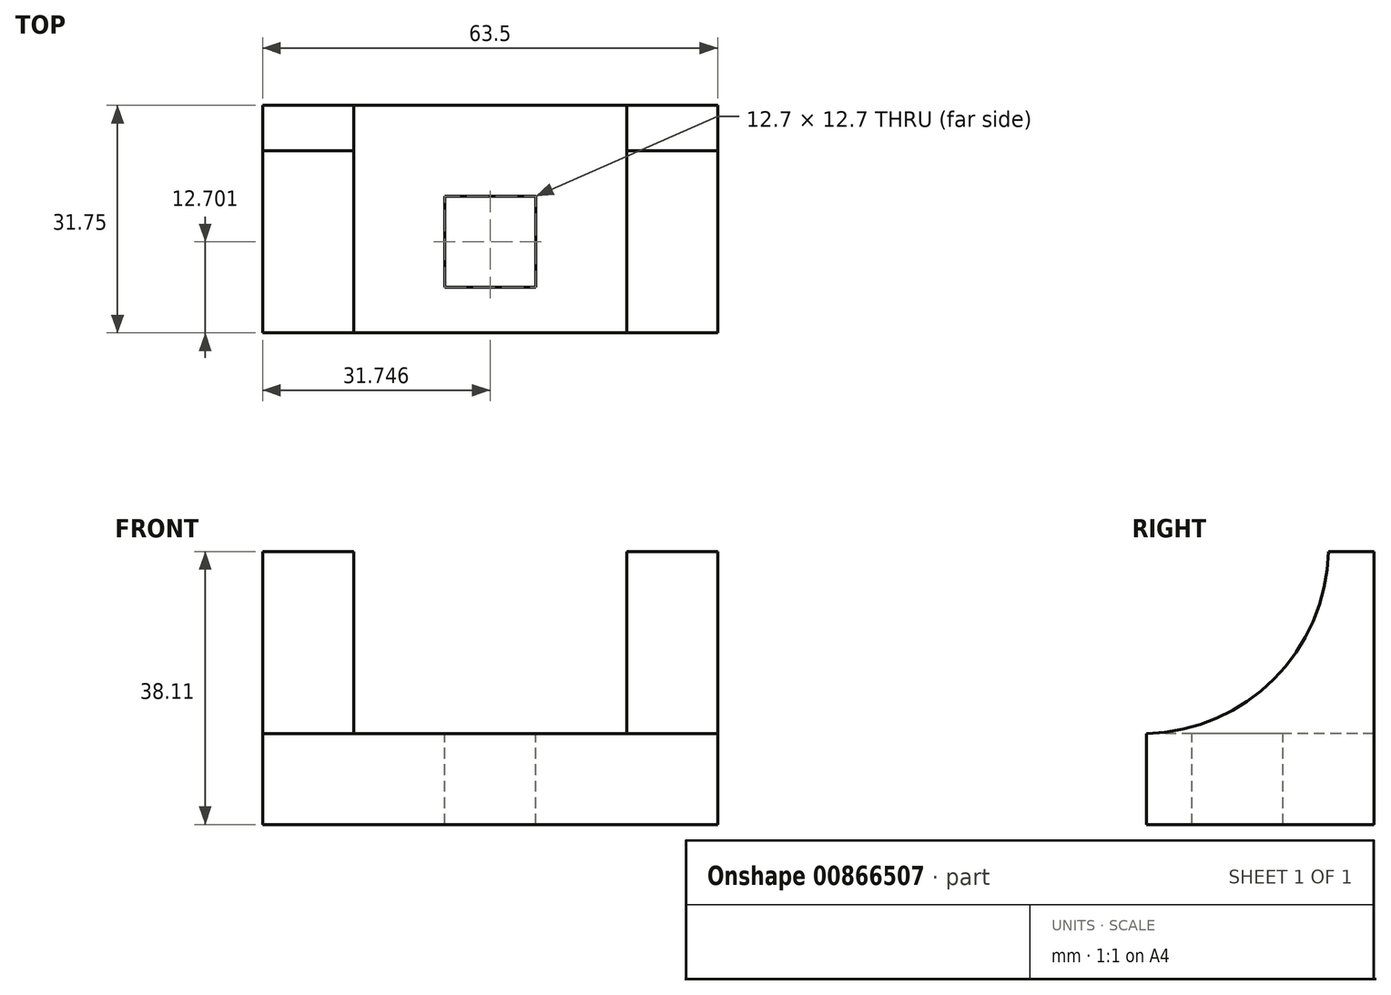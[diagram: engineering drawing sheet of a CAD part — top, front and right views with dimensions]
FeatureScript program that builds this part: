
annotation { "Feature Type Name" : "Feature", "Feature Type Description" : "" }
export const myFeature = defineFeature(function(context is Context, id is Id, definition is map)
    precondition{}
    {
        {
            var Q0;
            Q0=qCreatedBy(makeId("Top.planeOp"),FACE);
            var sketch = newSketch(context, id + "F0", { "sketchPlane" : qUnion([Q0])});
            skLineSegment(sketch, "E0.bottom", {"start": v(5.14, -12.72) * mm, "end": v(68.64, -12.72) * mm});
            skLineSegment(sketch, "E0.top", {"start": v(5.14, -44.47) * mm, "end": v(68.64, -44.47) * mm});
            skLineSegment(sketch, "E0.left", {"start": v(5.14, -12.72) * mm, "end": v(5.14, -44.47) * mm});
            skLineSegment(sketch, "E0.right", {"start": v(68.64, -12.72) * mm, "end": v(68.64, -44.47) * mm});
            skSolve(sketch);
        }
        {
            var Q0;
            Q0=makeQuery(id+"F0.imprint","IMPRINT",FACE,{"disambiguationData":[TD([[makeQuery(id+"F0.imprint","IMPRINT",EDGE,{"derivedFrom":sQuery(id+"F0.wireOp",EDGE,"E0.bottom")}),-1.0]])]});
            extrude(context, id + "F1", {"entities" : qUnion([Q0]), "depth" : 12.7 * mm, "offsetDistance" : 25.4 * mm});
        }
        {
            var Q0;
            Q0=makeQuery(id+"F1.opExtrude","SWEPT_FACE",FACE,{"disambiguationData":[OSD([sQuery(id+"F0.wireOp",EDGE,"E0.right")])]});
            var sketch = newSketch(context, id + "F2", { "sketchPlane" : qUnion([Q0])});
            skLineSegment(sketch, "E1", {"start": v(-12.72, 12.7) * mm, "end": v(-12.72, 38.1) * mm});
            skLineSegment(sketch, "E2", {"start": v(-12.72, 38.1) * mm, "end": v(-44.47, 38.1) * mm});
            skLineSegment(sketch, "E3", {"start": v(-44.47, 38.1) * mm, "end": v(-44.47, 12.7) * mm});
            skLineSegment(sketch, "E4", {"start": v(-44.47, 12.7) * mm, "end": v(-12.72, 12.7) * mm});
            skSolve(sketch);
        }
        {
            var Q0;
            Q0=makeQuery(id+"F1.opExtrude","SWEPT_FACE",FACE,{"disambiguationData":[OSD([sQuery(id+"F0.wireOp",EDGE,"E0.left")])]});
            var sketch = newSketch(context, id + "F3", { "sketchPlane" : qUnion([Q0])});
            skLineSegment(sketch, "E5", {"start": v(12.72, 12.7) * mm, "end": v(12.72, 38.1) * mm});
            skLineSegment(sketch, "E6", {"start": v(12.72, 38.1) * mm, "end": v(44.47, 38.1) * mm});
            skLineSegment(sketch, "E7", {"start": v(44.47, 38.1) * mm, "end": v(44.47, 12.7) * mm});
            skLineSegment(sketch, "E8", {"start": v(44.47, 12.7) * mm, "end": v(12.72, 12.7) * mm});
            skCircle(sketch, "E9", {"center": v(45.07, 38.7) * mm, "radius": 26.01 * mm});
            skPoint(sketch, "E9.third.point", {"position": v(61.03, 59.25) * mm});
            skSolve(sketch);
        }
        {
            var Q0;
            Q0 = qSketchRegion(id + "F3", true);
            extrude(context, id + "F4", {"entities" : qUnion([Q0]), "operationType" : NewBodyOperationType.ADD, "oppositeDirection" : true, "depth" : 12.7 * mm, "offsetDistance" : 25.4 * mm});
        }
        {
            var Q0;
            Q0 = qSketchRegion(id + "F2", true);
            extrude(context, id + "F5", {"entities" : qUnion([Q0]), "operationType" : NewBodyOperationType.ADD, "oppositeDirection" : true, "depth" : 12.7 * mm, "offsetDistance" : 25.4 * mm});
        }
        {
            var Q0;
            {var subQ0=sQuery(id+"F3.wireOp",EDGE,"E7");Q0=makeQuery(id+"F3.imprint","IMPRINT",FACE,{"disambiguationData":[TD([[makeQuery(id+"F3.imprint","IMPRINT",EDGE,{"derivedFrom":subQ0}),1.0]])]});}
            extrude(context, id + "F6", {"entities" : qUnion([Q0]), "operationType" : NewBodyOperationType.REMOVE, "oppositeDirection" : true, "depth" : 12.7 * mm, "offsetDistance" : 25.4 * mm});
        }
        {
            var Q0;
            {var subQ0=sQuery(id+"F3.wireOp",EDGE,"E7");Q0=makeQuery(id+"F3.imprint","IMPRINT",FACE,{"disambiguationData":[TD([[makeQuery(id+"F3.imprint","IMPRINT",EDGE,{"derivedFrom":subQ0}),-1.0]])]});}
            extrude(context, id + "F7", {"entities" : qUnion([Q0]), "operationType" : NewBodyOperationType.REMOVE, "oppositeDirection" : true, "depth" : 127 * mm, "offsetDistance" : 25.4 * mm});
        }
        {
            var Q0;
            Q0=makeQuery(id+"F1.opExtrude","CAP_FACE",FACE,{"disambiguationData":[OSD([sQuery(id+"F0.wireOp",EDGE,"E0.bottom"),sQuery(id+"F0.wireOp",EDGE,"E0.top"),sQuery(id+"F0.wireOp",EDGE,"E0.left"),sQuery(id+"F0.wireOp",EDGE,"E0.right")])],"isStart":false});
            var sketch = newSketch(context, id + "F8", { "sketchPlane" : qUnion([Q0])});
            skLineSegment(sketch, "E10.bottom", {"start": v(30.54, -25.42) * mm, "end": v(43.24, -25.42) * mm});
            skLineSegment(sketch, "E10.top", {"start": v(30.54, -38.12) * mm, "end": v(43.24, -38.12) * mm});
            skLineSegment(sketch, "E10.left", {"start": v(30.54, -25.42) * mm, "end": v(30.54, -38.12) * mm});
            skLineSegment(sketch, "E10.right", {"start": v(43.24, -25.42) * mm, "end": v(43.24, -38.12) * mm});
            skSolve(sketch);
        }
        {
            var Q0;
            Q0=makeQuery(id+"F8.imprint","IMPRINT",FACE,{"disambiguationData":[TD([[makeQuery(id+"F8.imprint","IMPRINT",EDGE,{"derivedFrom":sQuery(id+"F8.wireOp",EDGE,"E10.bottom")}),-1.0]])]});
            extrude(context, id + "F9", {"entities" : qUnion([Q0]), "operationType" : NewBodyOperationType.REMOVE, "oppositeDirection" : true, "depth" : 12.7 * mm, "offsetDistance" : 25.4 * mm});
        }
    });
